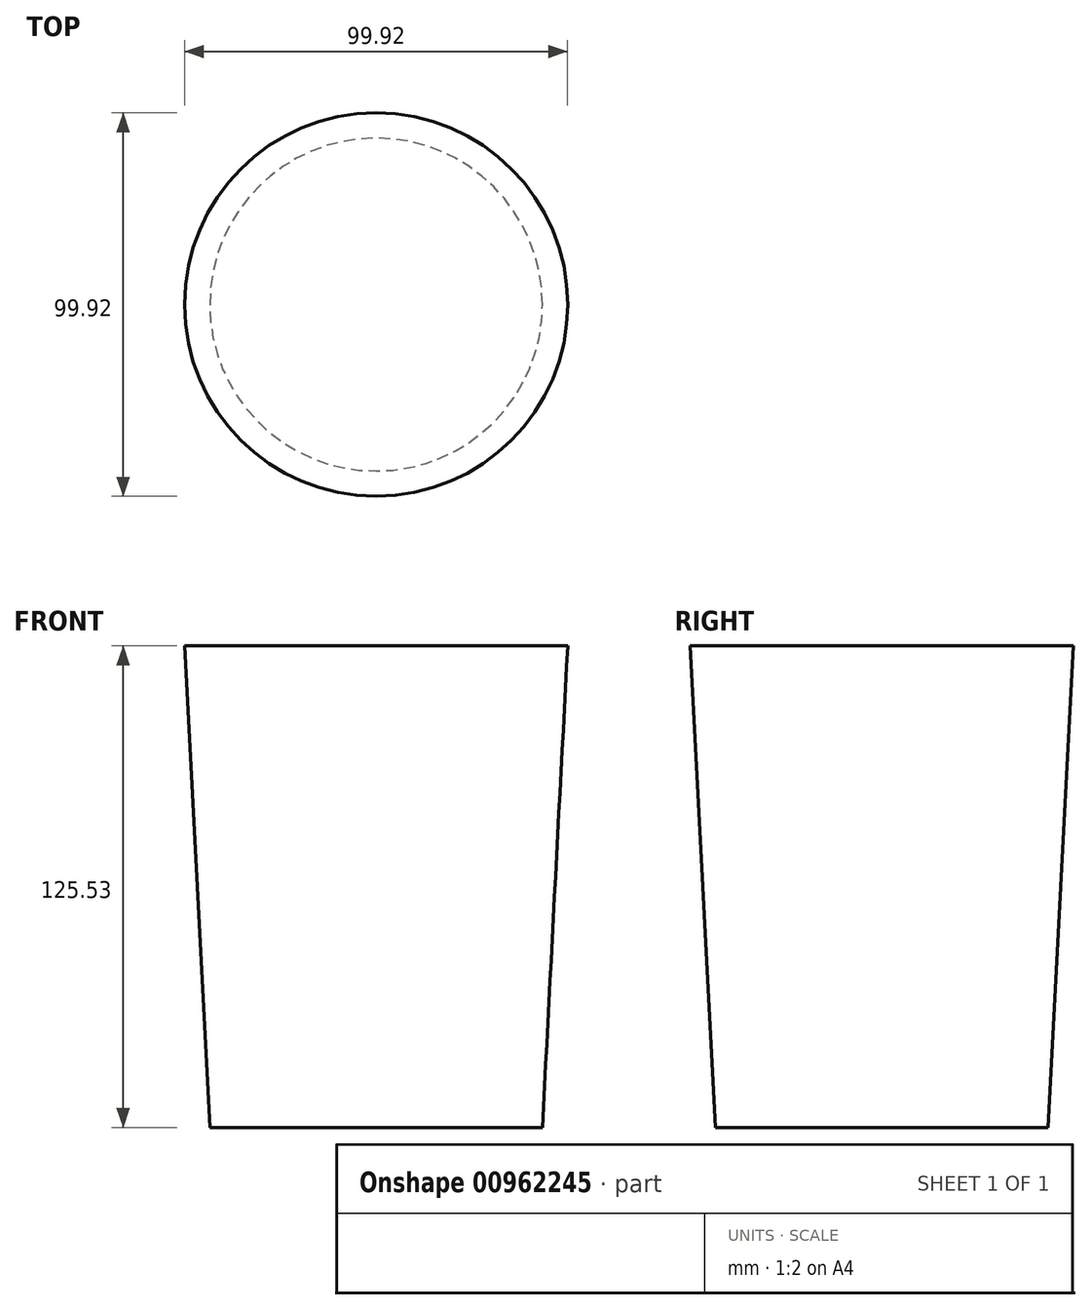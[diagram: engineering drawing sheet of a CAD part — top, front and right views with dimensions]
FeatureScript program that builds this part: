
annotation { "Feature Type Name" : "Feature", "Feature Type Description" : "" }
export const myFeature = defineFeature(function(context is Context, id is Id, definition is map)
    precondition{}
    {
        {
            var Q0;
            Q0=qCreatedBy(makeId("Top.planeOp"),FACE);
            var sketch = newSketch(context, id + "F0", { "sketchPlane" : qUnion([Q0])});
            skCircle(sketch, "E0", {"center": v(0, 0) * mm, "radius": 43.38 * mm});
            skSolve(sketch);
        }
        {
            var Q0;
            Q0=makeQuery(id+"F0.imprint","IMPRINT",FACE,{"disambiguationData":[TD([[makeQuery(id+"F0.imprint","IMPRINT",EDGE,{"derivedFrom":sQuery(id+"F0.wireOp",EDGE,"E0")}),1.0]])]});
            extrude(context, id + "F1", {"entities" : qUnion([Q0]), "depth" : 125.53 * mm, "offsetDistance" : 25.4 * mm, "hasDraft" : true, "draftAngle" : 3 * degree});
        }
    });
